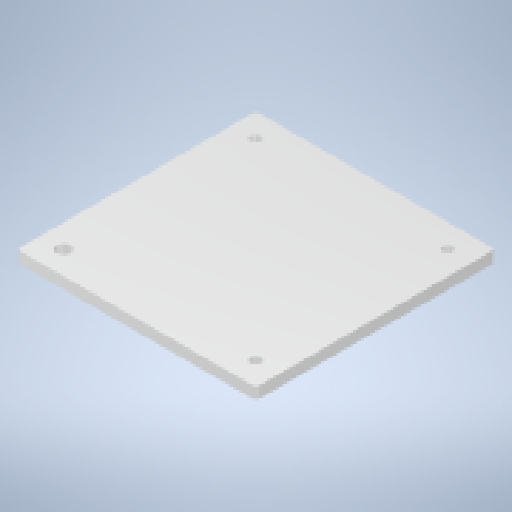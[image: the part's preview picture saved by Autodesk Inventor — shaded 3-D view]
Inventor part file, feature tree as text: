
AUTODESK INVENTOR PART (.ipt)
format: ipt  version: 2023.2 (Build 272271000, 271)  size: 155,648 bytes
history: native  units: mm
features: hole x2, sketch x1, extrude x1, fillet x1
ambient origin geometry x8: Origin, YZ Plane, XZ Plane, XY Plane, X Axis, Y Axis, Z Axis, Center Point
bodies: Solid1 (feature_tree)
feature tree (5):
  sketch  "Sketch1"  dims[d0=125.2mm d1=125.2mm d8=6.0mm d9=0.0mm d10=2.0mm d16=12.3mm d17=100.6mm d18=100.6mm d19=5.1mm d20=6.0mm d21=9.2mm d22=2.0mm d23=90.0deg d24=8.0mm d25=20.594885mm d26=7.2mm d27=6.0mm d28=12.25mm d29=2.0mm d30=90.0deg d31=8.0mm d32=20.594885mm]
  extrude  "Extrusion1"  Depth=125.2mm
  fillet  "Fillet1"  Radius=6.0mm
  hole  "Hole1"  [1 undecoded]
  hole  "Hole2"  [1 undecoded]
note: 2 required parameter values undecoded (feature->parameter linkage not recoverable at this tier; creation-order binding heuristic only, values carry confidence <= 0.55)
